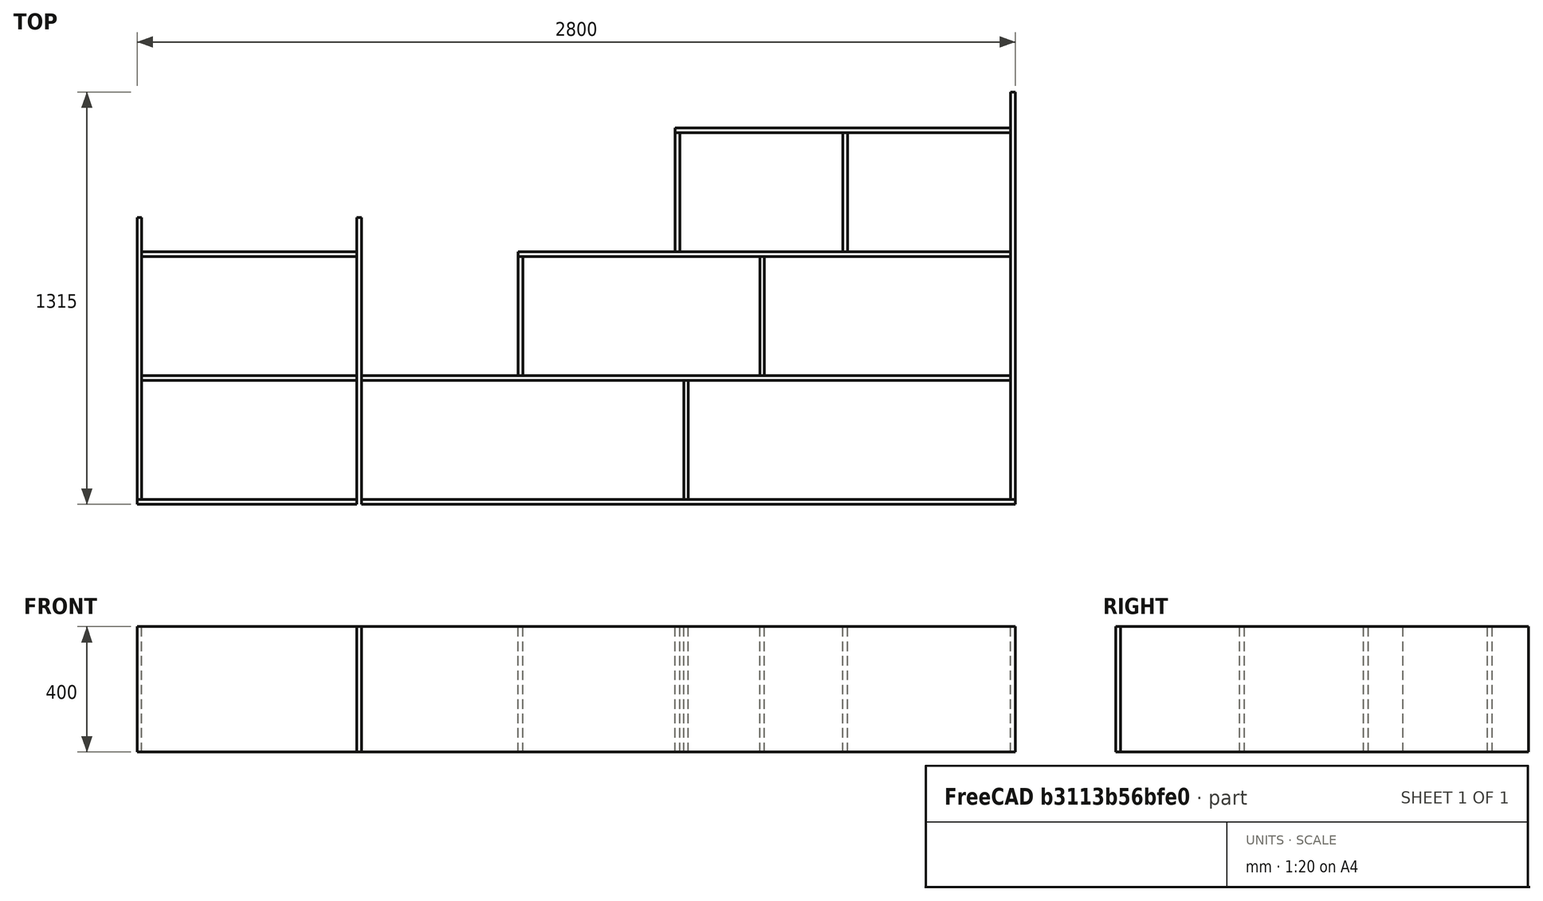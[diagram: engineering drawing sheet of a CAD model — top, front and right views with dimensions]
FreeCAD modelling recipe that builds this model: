
FCSTD DOCUMENT  (FreeCAD 0.18R16131 (Git))
Label: bibliotheque
License: All rights reserved
LicenseURL: http://en.wikipedia.org/wiki/All_rights_reserved
objects: TechDraw::DrawViewDimension×16, TechDraw::DrawViewPart×5, Sketcher::SketchObject×1, PartDesign::Body×1, Part::Extrusion×1, TechDraw::DrawSVGTemplate×1, TechDraw::DrawViewAnnotation×1, TechDraw::DrawPage×1
note: 3 computed .brp shape members not serialized (recipe doc carries the construction recipe); baked Part::Feature solids carry a one-line shape summary decoded from their .brp

FEATURE [Sketcher::SketchObject] Sketch
  MapMode = 5
  Support = -> [XY_Plane]
  sketch-geometry (60):
    g0: LineSegment StartX=0 StartY=0 StartZ=0 EndX=700 EndY=0 EndZ=0
    g1: LineSegment StartX=2800 StartY=15 StartZ=0 EndX=2800 EndY=1315 EndZ=0
    g2: LineSegment StartX=2800 StartY=1315 StartZ=0 EndX=2785 EndY=1315 EndZ=0
    g3: LineSegment StartX=2785 StartY=1315 StartZ=0 EndX=2785 EndY=15 EndZ=0
    g4: LineSegment StartX=2800 StartY=15 StartZ=0 EndX=715 EndY=15 EndZ=0
    g5: LineSegment StartX=715 StartY=-2e-16 StartZ=0 EndX=715 EndY=915 EndZ=0
    g6: LineSegment StartX=715 StartY=915 StartZ=0 EndX=700 EndY=915 EndZ=0
    g7: LineSegment StartX=700 StartY=915 StartZ=0 EndX=700 EndY=0 EndZ=0
    g8: LineSegment StartX=700 StartY=15 StartZ=0 EndX=0 EndY=15 EndZ=0
    g9: LineSegment StartX=15 StartY=15 StartZ=0 EndX=15 EndY=915 EndZ=0
    g10: LineSegment StartX=15 StartY=915 StartZ=0 EndX=0 EndY=915 EndZ=0
    g11: LineSegment StartX=0 StartY=915 StartZ=0 EndX=0 EndY=15 EndZ=0
    g12: LineSegment StartX=15 StartY=410 StartZ=0 EndX=700 EndY=410 EndZ=0
    g13: LineSegment StartX=700 StartY=410 StartZ=0 EndX=700 EndY=395 EndZ=0
    g14: LineSegment StartX=700 StartY=395 StartZ=0 EndX=15 EndY=395 EndZ=0
    g15: LineSegment StartX=15 StartY=395 StartZ=0 EndX=15 EndY=410 EndZ=0
    g16: LineSegment StartX=15 StartY=805 StartZ=0 EndX=700 EndY=805 EndZ=0
    g17: LineSegment StartX=700 StartY=805 StartZ=0 EndX=700 EndY=790 EndZ=0
    g18: LineSegment StartX=700 StartY=790 StartZ=0 EndX=15 EndY=790 EndZ=0
    g19: LineSegment StartX=15 StartY=790 StartZ=0 EndX=15 EndY=805 EndZ=0
    g20: LineSegment StartX=715 StartY=410 StartZ=0 EndX=2785 EndY=410 EndZ=0
    g21: LineSegment StartX=2785 StartY=410 StartZ=0 EndX=2785 EndY=395 EndZ=0
    g22: LineSegment StartX=2785 StartY=395 StartZ=0 EndX=715 EndY=395 EndZ=0
    g23: LineSegment StartX=715 StartY=395 StartZ=0 EndX=715 EndY=410 EndZ=0
    g24: LineSegment StartX=1215 StartY=410 StartZ=0 EndX=1215 EndY=790 EndZ=0
    g25: LineSegment StartX=1215 StartY=790 StartZ=0 EndX=1230 EndY=790 EndZ=0
    g26: LineSegment StartX=1230 StartY=790 StartZ=0 EndX=1230 EndY=410 EndZ=0
    g27: LineSegment StartX=1230 StartY=410 StartZ=0 EndX=1215 EndY=410 EndZ=0
    g28: LineSegment StartX=1215 StartY=790 StartZ=0 EndX=1215 EndY=805 EndZ=0
    g29: LineSegment StartX=1215 StartY=805 StartZ=0 EndX=2785 EndY=805 EndZ=0
    g30: LineSegment StartX=2785 StartY=805 StartZ=0 EndX=2785 EndY=790 EndZ=0
    g31: LineSegment StartX=2785 StartY=790 StartZ=0 EndX=1215 EndY=790 EndZ=0
    g32: LineSegment StartX=1985 StartY=790 StartZ=0 EndX=1985 EndY=410 EndZ=0
    g33: LineSegment StartX=1985 StartY=410 StartZ=0 EndX=2000 EndY=410 EndZ=0
    g34: LineSegment StartX=2000 StartY=410 StartZ=0 EndX=2000 EndY=790 EndZ=0
    g35: LineSegment StartX=2000 StartY=790 StartZ=0 EndX=1985 EndY=790 EndZ=0
    g36: LineSegment StartX=1715 StartY=1185 StartZ=0 EndX=1715 EndY=1200 EndZ=0
    g37: LineSegment StartX=1715 StartY=1200 StartZ=0 EndX=2785 EndY=1200 EndZ=0
    g38: LineSegment StartX=2785 StartY=1200 StartZ=0 EndX=2785 EndY=1185 EndZ=0
    g39: LineSegment StartX=2785 StartY=1185 StartZ=0 EndX=1715 EndY=1185 EndZ=0
    g40: LineSegment [constr] StartX=1215 StartY=805 StartZ=0 EndX=700 EndY=805 EndZ=0
    g41: LineSegment [constr] StartX=715 StartY=410 StartZ=0 EndX=715 EndY=395 EndZ=0
    g42: LineSegment StartX=0 StartY=15 StartZ=0 EndX=15 EndY=15 EndZ=0
    g43: LineSegment StartX=0 StartY=15 StartZ=0 EndX=0 EndY=0 EndZ=0
    g44: LineSegment StartX=2785 StartY=15 StartZ=0 EndX=2800 EndY=15 EndZ=0
    g45: LineSegment StartX=2800 StartY=15 StartZ=0 EndX=2800 EndY=0 EndZ=0
    g46: LineSegment StartX=1742.5 StartY=395 StartZ=0 EndX=1757.5 EndY=395 EndZ=0
    g47: LineSegment StartX=1757.5 StartY=395 StartZ=0 EndX=1757.5 EndY=15 EndZ=0
    g48: LineSegment StartX=1757.5 StartY=15 StartZ=0 EndX=1742.5 EndY=15 EndZ=0
    g49: LineSegment StartX=1742.5 StartY=15 StartZ=0 EndX=1742.5 EndY=395 EndZ=0
    g50: LineSegment StartX=1715 StartY=1185 StartZ=0 EndX=1730 EndY=1185 EndZ=0
    g51: LineSegment StartX=1730 StartY=1185 StartZ=0 EndX=1730 EndY=805 EndZ=0
    g52: LineSegment StartX=1730 StartY=805 StartZ=0 EndX=1715 EndY=805 EndZ=0
    g53: LineSegment StartX=1715 StartY=805 StartZ=0 EndX=1715 EndY=1185 EndZ=0
    g54: LineSegment StartX=2250 StartY=1185 StartZ=0 EndX=2265 EndY=1185 EndZ=0
    g55: LineSegment StartX=2265 StartY=1185 StartZ=0 EndX=2265 EndY=805 EndZ=0
    g56: LineSegment StartX=2265 StartY=805 StartZ=0 EndX=2250 EndY=805 EndZ=0
    g57: LineSegment StartX=2250 StartY=805 StartZ=0 EndX=2250 EndY=1185 EndZ=0
    g58: LineSegment [constr] StartX=715 StartY=410 StartZ=0 EndX=620.706 EndY=410 EndZ=0
    g59: LineSegment StartX=715 StartY=-2e-16 StartZ=0 EndX=2800 EndY=0 EndZ=0
  constraints (169):
    c: Horizontal(g0)
    c: Vertical(g1)
    c: Coincident(g1,g2)
    c: Horizontal(g2)
    c: Coincident(g2,g3)
    c: Vertical(g3)
    c: Horizontal(g4)
    c: Vertical(g5)
    c: Coincident(g5,g6)
    c: Horizontal(g6)
    c: Coincident(g6,g7)
    c: Vertical(g7)
    c: Horizontal(g8)
    c: Vertical(g9)
    c: Coincident(g9,g10)
    c: Coincident(g10,g11)
    c: Vertical(g11)
    c: PointOnObject(g12,g9)
    c: Horizontal(g12)
    c: Coincident(g12,g13)
    c: Vertical(g13)
    c: Coincident(g13,g14)
    c: PointOnObject(g14,g9)
    c: Horizontal(g14)
    c: Coincident(g14,g15)
    c: Coincident(g15,g12)
    c: PointOnObject(g16,g9)
    c: PointOnObject(g16,g7)
    c: Horizontal(g16)
    c: Coincident(g16,g17)
    c: PointOnObject(g17,g7)
    c: Coincident(g17,g18)
    c: Horizontal(g18)
    c: Coincident(g18,g19)
    c: Coincident(g19,g16)
    c: PointOnObject(g18,g9)
    c: PointOnObject(g20,g5)
    c: PointOnObject(g20,g3)
    c: Horizontal(g20)
    c: Coincident(g20,g21)
    c: PointOnObject(g21,g3)
    c: Coincident(g21,g22)
    c: PointOnObject(g22,g5)
    c: Horizontal(g22)
    c: Coincident(g22,g23)
    c: Coincident(g23,g20)
    c: Vertical(g24)
    c: Horizontal(g25)
    c: PointOnObject(g26,g20)
    c: Vertical(g26)
    c: Coincident(g26,g27)
    c: Coincident(g27,g24)
    c: Vertical(g28)
    c: PointOnObject(g29,g3)
    c: Horizontal(g29)
    c: Coincident(g29,g30)
    c: PointOnObject(g30,g3)
    c: Coincident(g30,g31)
    c: Coincident(g31,g28)
    c: Horizontal(g31)
    c: PointOnObject(g32,g20)
    c: Vertical(g32)
    c: Coincident(g32,g33)
    c: Coincident(g33,g34)
    c: PointOnObject(g34,g31)
    c: Vertical(g34)
    c: Coincident(g34,g35)
    c: Coincident(g35,g32)
    c: PointOnObject(g32,g31)
    c: Horizontal(g10)
    c: DistanceY(g11,g11) = 900
    c: DistanceX(g10,g10) = 15
    c: DistanceX(g2,g2) = 15
    c: DistanceY(g28,g28) = 15
    c: DistanceX(g25,g25) = 15
    c: PointOnObject(g33,g20)
    c: DistanceX(g32,g33) = 15
    c: DistanceY(g21,g20) = 15
    c: DistanceX(g6,g6) = 15
    c: DistanceY(g14,g12) = 15
    c: DistanceY(g18,g16) = 15
    c: DistanceY(g0,g8) = 15
    c: DistanceY(g59,g3) = 15
    c: DistanceY(g1,g1) = 1300
    c: DistanceX(g0,g59) = 2800
    c: DistanceX(g20,g24) = 500
    c: DistanceY(g4,g22) = 380
    c: Coincident(g29,g28)
    c: DistanceY(g26,g28) = 380
    c: PointOnObject(g37,g3)
    c: Horizontal(g37)
    c: Coincident(g37,g38)
    c: PointOnObject(g38,g3)
    c: Coincident(g38,g39)
    c: Coincident(g39,g36)
    c: Horizontal(g39)
    c: Vertical(g36)
    c: DistanceY(g38,g37) = 15
    c: DistanceX(g8,g7) = 700
    c: Coincident(g40,g28)
    c: Coincident(g40,g16)
    c: Horizontal(g40)
    c: Coincident(g41,g20)
    c: Coincident(g41,g22)
    c: Horizontal(g42)
    c: Coincident(g42,g11)
    c: Coincident(g42,g9)
    c: Coincident(g0,g-1)
    c: Coincident(g43,g8)
    c: Coincident(g43,g0)
    c: Vertical(g43)
    c: Coincident(g11,g8)
    c: Coincident(g44,g3)
    c: Coincident(g44,g1)
    c: Horizontal(g44)
    c: Coincident(g45,g4)
    c: Coincident(g45,g59)
    c: Vertical(g45)
    c: Coincident(g1,g4)
    c: PointOnObject(g46,g22)
    c: PointOnObject(g46,g22)
    c: Coincident(g46,g47)
    c: Vertical(g47)
    c: Coincident(g47,g48)
    c: PointOnObject(g48,g4)
    c: Coincident(g48,g49)
    c: Coincident(g49,g46)
    c: Vertical(g49)
    c: DistanceX(g48,g47) = 15
    c: Symmetric(g4,g1,g47)
    c: Symmetric(g24,g20,g33)
    c: Coincident(g36,g37)
    c: Coincident(g25,g24)
    c: Coincident(g25,g26)
    c: Coincident(g24,g28)
    c: DistanceY(g29,g38) = 380
    c: Coincident(g36,g50)
    c: PointOnObject(g50,g39)
    c: Coincident(g50,g51)
    c: PointOnObject(g51,g29)
    c: Vertical(g51)
    c: Coincident(g51,g52)
    c: PointOnObject(g52,g29)
    c: Coincident(g52,g53)
    c: Coincident(g53,g50)
    c: Vertical(g53)
    c: DistanceX(g28,g52) = 500
    c: DistanceX(g36,g50) = 15
    c: PointOnObject(g54,g39)
    c: PointOnObject(g54,g39)
    c: Coincident(g54,g55)
    c: PointOnObject(g55,g29)
    c: Vertical(g55)
    c: Coincident(g55,g56)
    c: Coincident(g56,g57)
    c: Coincident(g57,g54)
    c: Vertical(g57)
    c: DistanceX(g54,g54) = 15
    c: Symmetric(g52,g29,g56)
    c: PointOnObject(g12,g7)
    c: Coincident(g58,g20)
    c: Horizontal(g58)
    c: PointOnObject(g12,g58)
    c: PointOnObject(g8,g7)
    c: PointOnObject(g4,g5)
    c: PointOnObject(g0,g7)
    c: Coincident(g59,g5)
    c: Tangent(g0,g59)
    c: DistanceY(g8,g6) = 900
FEATURE [PartDesign::Body] Body
  Group = -> [Sketch]
  Origin = -> Origin
FEATURE [Part::Extrusion] Extrude001
  Base = -> Sketch
  Dir = (0,0,1)
  DirMode = 2
  FaceMakerClass = Part::FaceMakerBullseye
  LengthFwd = 400
  LengthRev = 0
  Solid = false
  Symmetric = false
FEATURE [TechDraw::DrawSVGTemplate] Template
  EditableTexts = Designed by Name=Yvan Labrit; Drawing number=Drawing number; FC-Date=Date; FC-SC=Scale; FC-SH=Sheet; FC-Title=Etageres Mesanine; Subtitle=Bois OSB 15 mn; Weight=Weight
  Height = 210
  Orientation = 1
  Width = 297
FEATURE [TechDraw::DrawViewPart] View
  CoarseView = false
  Direction = (0.292,0.281,0.914)
  Focus = 100
  HardHidden = false
  IsoCount = 0
  IsoHidden = false
  IsoVisible = false
  LockPosition = false
  Perspective = false
  Rotation = -120
  Scale = 0.04
  ScaleType = 0
  SeamHidden = false
  SeamVisible = false
  SmoothHidden = false
  SmoothVisible = false
  Source = -> [Extrude001]
  X = 78.7603
  Y = 49.5911
FEATURE [TechDraw::DrawViewPart] View001
  CoarseView = true
  Direction = (0,0,1)
  Focus = 100
  HardHidden = false
  IsoCount = 0
  IsoHidden = false
  IsoVisible = false
  LockPosition = false
  Perspective = false
  Rotation = 0
  Scale = 0.04
  ScaleType = 0
  SeamHidden = false
  SeamVisible = false
  SmoothHidden = false
  SmoothVisible = false
  Source = -> [Extrude001]
  X = 102.132
  Y = 152.088
FEATURE [TechDraw::DrawViewPart] View003
  CoarseView = false
  Direction = (0,1,0)
  Focus = 100
  HardHidden = false
  IsoCount = 0
  IsoHidden = false
  IsoVisible = false
  LockPosition = false
  Perspective = false
  Rotation = 180
  Scale = 0.04
  ScaleType = 0
  SeamHidden = false
  SeamVisible = false
  SmoothHidden = false
  SmoothVisible = false
  Source = -> [Extrude001]
  X = 102.012
  Y = 99.5329
FEATURE [TechDraw::DrawViewPart] View004
  CoarseView = false
  Direction = (1,0,0)
  Focus = 100
  HardHidden = false
  IsoCount = 0
  IsoHidden = false
  IsoVisible = false
  LockPosition = false
  Perspective = false
  Rotation = -90
  Scale = 0.04
  ScaleType = 0
  SeamHidden = false
  SeamVisible = false
  SmoothHidden = false
  SmoothVisible = false
  Source = -> [Extrude001]
  X = 180.9
  Y = 153.24
FEATURE [TechDraw::DrawViewPart] View005
  CoarseView = false
  Direction = (-1,0,0)
  Focus = 100
  HardHidden = false
  IsoCount = 0
  IsoHidden = false
  IsoVisible = false
  LockPosition = false
  Perspective = false
  Rotation = 90
  Scale = 0.04
  ScaleType = 0
  SeamHidden = false
  SeamVisible = false
  SmoothHidden = false
  SmoothVisible = false
  Source = -> [Extrude001]
  X = 23.6864
  Y = 152.13
FEATURE [TechDraw::DrawViewDimension] Dimension
  Arbitrary = false
  FormatSpec = %.2f
  LockPosition = false
  MeasureType = 1
  OverTolerance = 0
  References2D = -> [View001]
  Rotation = 0
  ScaleType = 0
  Type = 1
  UnderTolerance = 0
  X = -43.0958
  Y = -34.3517
FEATURE [TechDraw::DrawViewDimension] Dimension001
  Arbitrary = false
  FormatSpec = %.2f
  LockPosition = false
  MeasureType = 1
  OverTolerance = 0
  References2D = -> [View001]
  Rotation = 0
  ScaleType = 0
  Type = 1
  UnderTolerance = 0
  X = -1.45735
  Y = -34.3517
FEATURE [TechDraw::DrawViewDimension] Dimension002
  Arbitrary = false
  FormatSpec = %.2f
  LockPosition = false
  MeasureType = 1
  OverTolerance = 0
  References2D = -> [View001]
  Rotation = 0
  ScaleType = 0
  Type = 2
  UnderTolerance = 0
  X = -66.4134
  Y = 20.8192
FEATURE [TechDraw::DrawViewDimension] Dimension003
  Arbitrary = false
  FormatSpec = %.2f
  LockPosition = false
  MeasureType = 1
  OverTolerance = 0
  References2D = -> [View001]
  Rotation = 0
  ScaleType = 0
  Type = 2
  UnderTolerance = 0
  X = -38.9943
  Y = 17.3188
FEATURE [TechDraw::DrawViewDimension] Dimension004
  Arbitrary = false
  FormatSpec = %.2f
  LockPosition = false
  MeasureType = 1
  OverTolerance = 0
  References2D = -> [View001]
  Rotation = 0
  ScaleType = 0
  Type = 2
  UnderTolerance = 0
  X = -17.7889
  Y = -1.36838
FEATURE [TechDraw::DrawViewDimension] Dimension005
  Arbitrary = false
  FormatSpec = %.2f
  LockPosition = false
  MeasureType = 1
  OverTolerance = 0
  References2D = -> [View001]
  Rotation = 0
  ScaleType = 0
  Type = 1
  UnderTolerance = 0
  X = -42.1561
  Y = 0.282607
FEATURE [TechDraw::DrawViewDimension] Dimension006
  Arbitrary = false
  FormatSpec = %.2f
  LockPosition = false
  MeasureType = 1
  OverTolerance = 0
  References2D = -> [View001]
  Rotation = 0
  ScaleType = 0
  Type = 1
  UnderTolerance = 0
  X = 29.4387
  Y = 35.6119
FEATURE [TechDraw::DrawViewDimension] Dimension007
  Arbitrary = false
  FormatSpec = %.2f
  LockPosition = false
  MeasureType = 1
  OverTolerance = 0
  References2D = -> [View001]
  Rotation = 0
  ScaleType = 0
  Type = 1
  UnderTolerance = 0
  X = 2.10592
  Y = 28.2502
FEATURE [TechDraw::DrawViewDimension] Dimension008
  Arbitrary = false
  FormatSpec = %.2f
  LockPosition = false
  MeasureType = 1
  OverTolerance = 0
  References2D = -> [View001]
  Rotation = 0
  ScaleType = 0
  Type = 1
  UnderTolerance = 0
  X = -16.7885
  Y = 19.5202
FEATURE [TechDraw::DrawViewDimension] Dimension009
  Arbitrary = false
  FormatSpec = %.2f
  LockPosition = false
  MeasureType = 1
  OverTolerance = 0
  References2D = -> [View004]
  Rotation = 0
  ScaleType = 0
  Type = 1
  UnderTolerance = 0
  X = 23.5257
  Y = -42.98
FEATURE [TechDraw::DrawViewDimension] Dimension010
  Arbitrary = false
  FormatSpec = %.2f
  LockPosition = false
  MeasureType = 1
  OverTolerance = 0
  References2D = -> [View003]
  Rotation = 0
  ScaleType = 0
  Type = 1
  UnderTolerance = 0
  X = -8.47086
  Y = -14.5428
FEATURE [TechDraw::DrawViewDimension] Dimension011
  Arbitrary = false
  FormatSpec = %.2f
  LockPosition = false
  MeasureType = 1
  OverTolerance = 0
  References2D = -> [View003]
  Rotation = 0
  ScaleType = 0
  Type = 1
  UnderTolerance = 0
  X = -17.5673
  Y = -0.051554
FEATURE [TechDraw::DrawViewDimension] Dimension012
  Arbitrary = false
  FormatSpec = %.2f
  LockPosition = false
  MeasureType = 1
  OverTolerance = 0
  References2D = -> [View001]
  Rotation = 0
  ScaleType = 0
  Type = 1
  UnderTolerance = 0
  X = 35.6008
  Y = -28.9279
FEATURE [TechDraw::DrawViewDimension] Dimension013
  Arbitrary = false
  FormatSpec = %.2f
  LockPosition = false
  MeasureType = 1
  OverTolerance = 0
  References2D = -> [View001]
  Rotation = 0
  ScaleType = 0
  Type = 1
  UnderTolerance = 0
  X = 39.2352
  Y = -0.894086
FEATURE [TechDraw::DrawViewDimension] Dimension014
  Arbitrary = false
  FormatSpec = %.2f
  LockPosition = false
  MeasureType = 1
  OverTolerance = 0
  References2D = -> [View001]
  Rotation = 0
  ScaleType = 0
  Type = 2
  UnderTolerance = 0
  X = 61.4217
  Y = 0.059037
FEATURE [TechDraw::DrawViewDimension] Dimension015
  Arbitrary = false
  FormatSpec = %.2f
  LockPosition = false
  MeasureType = 1
  OverTolerance = 0
  References2D = -> [View001]
  Rotation = 0
  ScaleType = 0
  Type = 1
  UnderTolerance = 0
  X = 47.1614
  Y = 12.524
FEATURE [TechDraw::DrawViewAnnotation] Annotation
  Font = MS Shell Dlg 2
  LineSpace = 80
  LockPosition = false
  MaxWidth = -1
  Rotation = 0
  ScaleType = 0
  Text = Horizontal | 2 x 40 x 68.50 | 1 x 40 x 70.00 | 1 x 40 x 208.50 | 1 x 40 x 207.00 | 1 x 40 x 157.00 | 1 x 40 x 107.00 | Vertical | 1 x 40 x 90.00 | 1 x 40 x 91.50 | 5 x 40 x 38.00 | Epaisseur 15 mn
  TextSize = 5
  TextStyle = 0
  X = 250.964
  Y = 138.17
FEATURE [TechDraw::DrawPage] Page
  KeepUpdated = true
  ProjectionType = 0
  Template = -> Template
  Views = -> [View,View001,View003,View004,View005,Dimension,Dimension001,Dimension002,Dimension003,Dimension004,Dimension005,Dimension006,Dimension007,Dimension008,Dimension009,Dimension010,Dimension011,Dimension012,Dimension013,Dimension014,Dimension015,Annotation]
